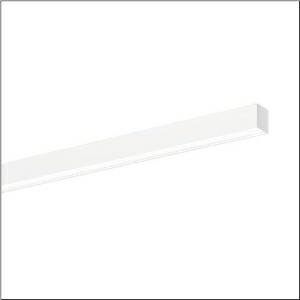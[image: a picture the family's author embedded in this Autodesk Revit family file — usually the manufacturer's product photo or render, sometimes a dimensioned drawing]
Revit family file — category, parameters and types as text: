
# Revit family: silica_r__21_51mx23da34wb_c22c
name_source: partatom
category: Lighting Fixtures
units: mm (PartAtom-declared; Revit-internal decimal feet)

## family parameters
Cut with Voids When Loaded = No
Host = Face
Light Source = No
Part Type = Normal
Room Calculation Point = No
Round Connector Dimension = Use Diameter
Shared = No

## types (1)
- --- (1 x LED, 3280 lm, 24.1 W, 3000K)
    Apparent Load = 24 VA
    CIE Flux Codes = 78 96 99 100 100
    Color Rendering = 80
    Color Temperature = 3000K
    Default Elevation = 1800 mm
    Description = Silica® 21, office luminaire, primary optical cover: prismatic diffuser, of PMMA, CAT 2 (L<= 3000cd/m²), light emission: direct distribution, primary light characteristic: symmetric, installation type: surface-mounted, LED, rated luminous flux: 3.280lm, luminous efficacy: 136lm/W, light colour: 830, colour temperature: 3000K, control gear: DALI 2, with terminal, 3+2-pole, max. 2.5mm², mains connection: 220..240V, AC, 50/60Hz, rated input power: 24.1W, luminaire housing, of aluminium, traffic white (RAL 9016), length: 1.204mm, width: 53mm, height: 53mm, protection rating (complete): IP20, insulation class (complete): insulation class I (protective earthing), certification: CE, permissible operating ambient temperature: 0..+35°C, standard: EN 50419, packaging unit: 1 piece
    Height = 53 mm
    Lamp = 1 x LED
    Lamp Light Flux = 3280 lm
    Lamp Power = 24.1 W
    Lamp count = 1
    Length = 1204 mm
    Luminous efficacy = 136 lm/W
    Manufacturer = Siteco
    ModVariant = No
    Model = 51MX23DA34WB
    Mounting Place = Ceiling
    Mounting Type = Surface mounted
    Number of Poles = 1
    OnlyDefault = Yes
    Power Factor = 1
    Product Name = Silica® 21
    Product group = office luminaire | ceiling mounted
    ProductGroupID = 303
    Protection Class = Protection class I
    Protection Degree = IP 20
    RLX_Detail_Level = 1
    RLX_Emergency_Light_Flux = 0 lm
    RLX_Emergency_Type = 0
    RLX_Emergency_Type_DB = No
    RlxData = <blob elided: 18901 chars, md5=52d61a73>
    Socket = socket
    Standby Power = 0 W
    System Light Flux = 3280 lm
    System Power = 24 W
    Type Comments = factory setting: luminous flux: 100 % | dim-lin: 254 | 345 mA
    Type Image = l_1335877.jpg
    URL = http://relux.com
    VarID = @adj_027119
    Voltage = 0 V
    Weight = 0.00 kg
    Width = 53 mm

## geometry (parser evidence)
native form markers: Blend x4, Sweep x12
no freeform markers — native parametric forms only
